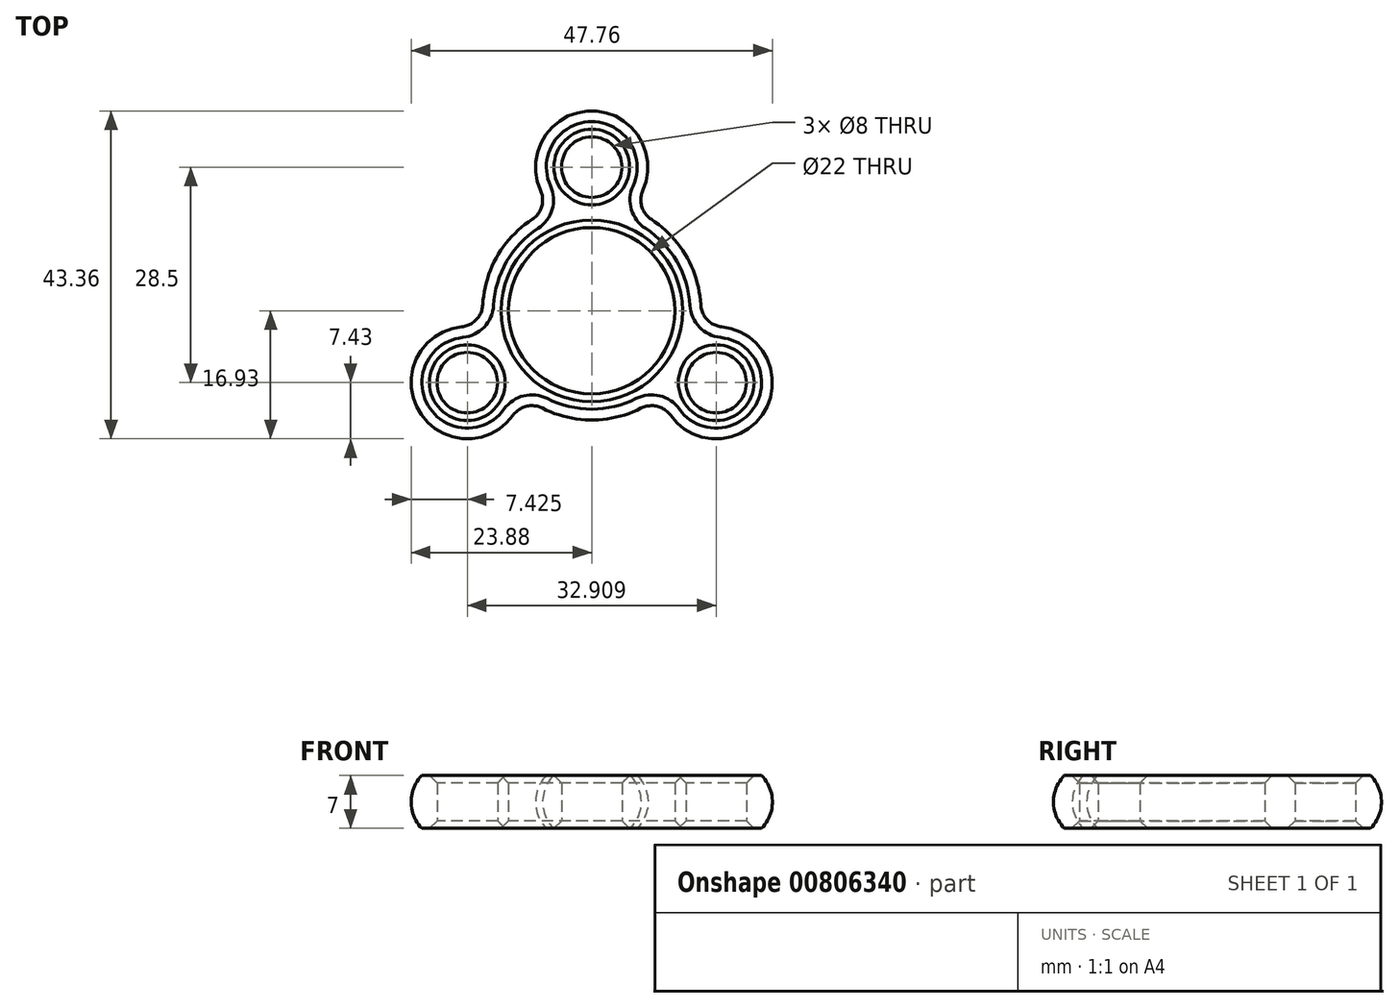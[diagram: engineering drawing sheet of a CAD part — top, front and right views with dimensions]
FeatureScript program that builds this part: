
annotation { "Feature Type Name" : "Feature", "Feature Type Description" : "" }
export const myFeature = defineFeature(function(context is Context, id is Id, definition is map)
    precondition{}
    {
        {
            var Q0;
            Q0=qCreatedBy(makeId("Top.planeOp"),FACE);
            var sketch = newSketch(context, id + "F0", { "sketchPlane" : qUnion([Q0])});
            skCircle(sketch, "E0", {"center": v(0, 0) * mm, "radius": 11 * mm});
            skCircle(sketch, "E1", {"center": v(0, 0) * mm, "radius": 13 * mm});
            skCircle(sketch, "E2", {"center": v(0, 19) * mm, "radius": 4 * mm});
            skCircle(sketch, "E3", {"center": v(0, 19) * mm, "radius": 6 * mm});
            skCircle(sketch, "E4.1.0", {"center": v(-16.45, -9.5) * mm, "radius": 6 * mm});
            skCircle(sketch, "E4.1.1", {"center": v(-16.45, -9.5) * mm, "radius": 4 * mm});
            skCircle(sketch, "E4.2.0", {"center": v(16.45, -9.5) * mm, "radius": 6 * mm});
            skCircle(sketch, "E4.2.1", {"center": v(16.45, -9.5) * mm, "radius": 4 * mm});
            skCircle(sketch, "E5", {"center": v(-9.56, 14.66) * mm, "radius": 4.5 * mm});
            skCircle(sketch, "E6", {"center": v(9.56, 14.66) * mm, "radius": 4.5 * mm});
            skCircle(sketch, "E7.1.0", {"center": v(-7.91, -15.6) * mm, "radius": 4.5 * mm});
            skCircle(sketch, "E7.1.1", {"center": v(-17.47, 0.95) * mm, "radius": 4.5 * mm});
            skCircle(sketch, "E7.2.0", {"center": v(17.47, 0.95) * mm, "radius": 4.5 * mm});
            skCircle(sketch, "E7.2.1", {"center": v(7.91, -15.6) * mm, "radius": 4.5 * mm});
            skSolve(sketch);
        }
        {
            var Q0;
            {var subQ0=sQuery(id+"F0.wireOp",EDGE,"E6");var subQ1=sQuery(id+"F0.wireOp",EDGE,"E1");var subQ2=makeQuery(id+"F0.imprint","INTERSECT",VERTEX,{"derivedFrom":[subQ1,subQ0]});Q0=makeQuery(id+"F0.imprint","IMPRINT",FACE,{"disambiguationData":[TD([[makeQuery(id+"F0.imprint","IMPRINT",EDGE,{"disambiguationData":[TD([[subQ2,-1.0]])],"derivedFrom":subQ1}),-1.0]])]});}
            var Q1;
            {var subQ0=sQuery(id+"F0.wireOp",EDGE,"E3");var subQ1=sQuery(id+"F0.wireOp",EDGE,"E1");var subQ2=makeQuery(id+"F0.imprint","INTERSECT",VERTEX,{"derivedFrom":[subQ1,subQ0]});Q1=makeQuery(id+"F0.imprint","IMPRINT",FACE,{"disambiguationData":[TD([[makeQuery(id+"F0.imprint","IMPRINT",EDGE,{"disambiguationData":[TD([[subQ2,-1.0]])],"derivedFrom":subQ1}),-1.0]])]});}
            var Q2;
            {var subQ0=sQuery(id+"F0.wireOp",EDGE,"E7.1.1");var subQ1=sQuery(id+"F0.wireOp",EDGE,"E1");var subQ2=makeQuery(id+"F0.imprint","INTERSECT",VERTEX,{"derivedFrom":[subQ1,subQ0]});Q2=makeQuery(id+"F0.imprint","IMPRINT",FACE,{"disambiguationData":[TD([[makeQuery(id+"F0.imprint","IMPRINT",EDGE,{"disambiguationData":[TD([[subQ2,-1.0]])],"derivedFrom":subQ1}),-1.0]])]});}
            var Q3;
            {var subQ0=sQuery(id+"F0.wireOp",EDGE,"E4.1.0");var subQ1=sQuery(id+"F0.wireOp",EDGE,"E1");var subQ2=makeQuery(id+"F0.imprint","INTERSECT",VERTEX,{"derivedFrom":[subQ1,subQ0]});Q3=makeQuery(id+"F0.imprint","IMPRINT",FACE,{"disambiguationData":[TD([[makeQuery(id+"F0.imprint","IMPRINT",EDGE,{"disambiguationData":[TD([[subQ2,-1.0]])],"derivedFrom":subQ1}),-1.0]])]});}
            var Q4;
            {var subQ0=sQuery(id+"F0.wireOp",EDGE,"E7.2.1");var subQ1=sQuery(id+"F0.wireOp",EDGE,"E1");var subQ2=makeQuery(id+"F0.imprint","INTERSECT",VERTEX,{"derivedFrom":[subQ1,subQ0]});Q4=makeQuery(id+"F0.imprint","IMPRINT",FACE,{"disambiguationData":[TD([[makeQuery(id+"F0.imprint","IMPRINT",EDGE,{"disambiguationData":[TD([[subQ2,-1.0]])],"derivedFrom":subQ1}),-1.0]])]});}
            var Q5;
            {var subQ0=sQuery(id+"F0.wireOp",EDGE,"E7.2.0");var subQ1=sQuery(id+"F0.wireOp",EDGE,"E1");var subQ2=makeQuery(id+"F0.imprint","INTERSECT",VERTEX,{"derivedFrom":[subQ1,subQ0]});Q5=makeQuery(id+"F0.imprint","IMPRINT",FACE,{"disambiguationData":[TD([[makeQuery(id+"F0.imprint","IMPRINT",EDGE,{"disambiguationData":[TD([[subQ2,1.0]])],"derivedFrom":subQ1}),-1.0]])]});}
            var Q6;
            Q6=makeQuery(id+"F0.imprint","IMPRINT",FACE,{"disambiguationData":[TD([[makeQuery(id+"F0.imprint","IMPRINT",EDGE,{"derivedFrom":sQuery(id+"F0.wireOp",EDGE,"E0")}),-1.0]])]});
            var Q7;
            Q7=makeQuery(id+"F0.imprint","IMPRINT",FACE,{"disambiguationData":[TD([[makeQuery(id+"F0.imprint","IMPRINT",EDGE,{"derivedFrom":sQuery(id+"F0.wireOp",EDGE,"E2")}),-1.0]])]});
            var Q8;
            Q8=makeQuery(id+"F0.imprint","IMPRINT",FACE,{"disambiguationData":[TD([[makeQuery(id+"F0.imprint","IMPRINT",EDGE,{"derivedFrom":sQuery(id+"F0.wireOp",EDGE,"E4.1.1")}),-1.0]])]});
            var Q9;
            Q9=makeQuery(id+"F0.imprint","IMPRINT",FACE,{"disambiguationData":[TD([[makeQuery(id+"F0.imprint","IMPRINT",EDGE,{"derivedFrom":sQuery(id+"F0.wireOp",EDGE,"E4.2.1")}),-1.0]])]});
            extrude(context, id + "F1", {"entities" : qUnion([Q0, Q1, Q2, Q3, Q4, Q5, Q6, Q7, Q8, Q9]), "endBound" : BoundingType.SYMMETRIC, "depth" : 7 * mm, "offsetDistance" : 25.4 * mm});
        }
        {
            var Q0;
            Q0=qCreatedBy(makeId("Right.planeOp"),FACE);
            var sketch = newSketch(context, id + "F2", { "sketchPlane" : qUnion([Q0])});
            skLineSegment(sketch, "E8", {"start": v(25, 3.5) * mm, "end": v(25, -3.5) * mm});
            skArc(sketch, "E9", {"start": v(25, -3.5) * mm, "mid": v(26.43, 0) * mm, "end": v(25, 3.5) * mm});
            skSolve(sketch);
        }
        {
            var Q0;
            Q0=makeQuery(id+"F2.imprint","IMPRINT",FACE,{"disambiguationData":[TD([[makeQuery(id+"F2.imprint","IMPRINT",EDGE,{"derivedFrom":sQuery(id+"F2.wireOp",EDGE,"E8")}),1.0]])]});
            var Q1;
            Q1=makeQuery(id+"F1.opExtrude","CAP_EDGE",EDGE,{"disambiguationData":[OSD([sQuery(id+"F0.wireOp",EDGE,"E3")])],"isStart":false});
            var Q2;
            Q2=makeQuery(id+"F1.opExtrude","CAP_EDGE",EDGE,{"disambiguationData":[OSD([sQuery(id+"F0.wireOp",EDGE,"E5")])],"isStart":false});
            var Q3;
            {var subQ0=sQuery(id+"F0.wireOp",EDGE,"E1");Q3=makeQuery(id+"F1.opExtrude","CAP_EDGE",EDGE,{"disambiguationData":[OSD([subQ0]),TDD([makeQuery(id+"F0.imprint","IMPRINT",EDGE,{"disambiguationData":[TD([[makeQuery(id+"F0.imprint","INTERSECT",VERTEX,{"derivedFrom":[subQ0,sQuery(id+"F0.wireOp",EDGE,"E5")]}),-1.0]])],"derivedFrom":subQ0})])],"isStart":false});}
            var Q4;
            Q4=makeQuery(id+"F1.opExtrude","CAP_EDGE",EDGE,{"disambiguationData":[OSD([sQuery(id+"F0.wireOp",EDGE,"E7.1.1")])],"isStart":false});
            var Q5;
            Q5=makeQuery(id+"F1.opExtrude","CAP_EDGE",EDGE,{"disambiguationData":[OSD([sQuery(id+"F0.wireOp",EDGE,"E4.1.0")])],"isStart":false});
            var Q6;
            Q6=makeQuery(id+"F1.opExtrude","CAP_EDGE",EDGE,{"disambiguationData":[OSD([sQuery(id+"F0.wireOp",EDGE,"E7.1.0")])],"isStart":false});
            var Q7;
            {var subQ0=sQuery(id+"F0.wireOp",EDGE,"E1");Q7=makeQuery(id+"F1.opExtrude","CAP_EDGE",EDGE,{"disambiguationData":[OSD([subQ0]),TDD([makeQuery(id+"F0.imprint","IMPRINT",EDGE,{"disambiguationData":[TD([[makeQuery(id+"F0.imprint","INTERSECT",VERTEX,{"derivedFrom":[subQ0,sQuery(id+"F0.wireOp",EDGE,"E7.1.0")]}),-1.0]])],"derivedFrom":subQ0})])],"isStart":false});}
            var Q8;
            Q8=makeQuery(id+"F1.opExtrude","CAP_EDGE",EDGE,{"disambiguationData":[OSD([sQuery(id+"F0.wireOp",EDGE,"E7.2.1")])],"isStart":false});
            var Q9;
            Q9=makeQuery(id+"F1.opExtrude","CAP_EDGE",EDGE,{"disambiguationData":[OSD([sQuery(id+"F0.wireOp",EDGE,"E4.2.0")])],"isStart":false});
            var Q10;
            Q10=makeQuery(id+"F1.opExtrude","CAP_EDGE",EDGE,{"disambiguationData":[OSD([sQuery(id+"F0.wireOp",EDGE,"E7.2.0")])],"isStart":false});
            var Q11;
            {var subQ0=sQuery(id+"F0.wireOp",EDGE,"E1");Q11=makeQuery(id+"F1.opExtrude","CAP_EDGE",EDGE,{"disambiguationData":[OSD([subQ0]),TDD([makeQuery(id+"F0.imprint","IMPRINT",EDGE,{"disambiguationData":[TD([[makeQuery(id+"F0.imprint","INTERSECT",VERTEX,{"derivedFrom":[subQ0,sQuery(id+"F0.wireOp",EDGE,"E6")]}),1.0]])],"derivedFrom":subQ0})])],"isStart":false});}
            var Q12;
            Q12=makeQuery(id+"F1.opExtrude","CAP_EDGE",EDGE,{"disambiguationData":[OSD([sQuery(id+"F0.wireOp",EDGE,"E6")])],"isStart":false});
            sweep(context, id + "F3", {"operationType" : NewBodyOperationType.ADD, "profiles" : qUnion([Q0]), "path" : qUnion([Q1, Q2, Q3, Q4, Q5, Q6, Q7, Q8, Q9, Q10, Q11, Q12])});
        }
        {
            var Q0;
            Q0=makeQuery(id+"F1.opExtrude","CAP_EDGE",EDGE,{"disambiguationData":[OSD([sQuery(id+"F0.wireOp",EDGE,"E2")])],"isStart":false});
            var Q1;
            Q1=makeQuery(id+"F1.opExtrude","CAP_EDGE",EDGE,{"disambiguationData":[OSD([sQuery(id+"F0.wireOp",EDGE,"E0")])],"isStart":false});
            var Q2;
            Q2=makeQuery(id+"F1.opExtrude","CAP_EDGE",EDGE,{"disambiguationData":[OSD([sQuery(id+"F0.wireOp",EDGE,"E4.1.1")])],"isStart":false});
            var Q3;
            Q3=makeQuery(id+"F1.opExtrude","CAP_EDGE",EDGE,{"disambiguationData":[OSD([sQuery(id+"F0.wireOp",EDGE,"E4.2.1")])],"isStart":false});
            var Q4;
            Q4=makeQuery(id+"F1.opExtrude","CAP_EDGE",EDGE,{"disambiguationData":[OSD([sQuery(id+"F0.wireOp",EDGE,"E4.1.1")])],"isStart":true});
            var Q5;
            Q5=makeQuery(id+"F1.opExtrude","CAP_EDGE",EDGE,{"disambiguationData":[OSD([sQuery(id+"F0.wireOp",EDGE,"E0")])],"isStart":true});
            var Q6;
            Q6=makeQuery(id+"F1.opExtrude","CAP_EDGE",EDGE,{"disambiguationData":[OSD([sQuery(id+"F0.wireOp",EDGE,"E4.2.1")])],"isStart":true});
            var Q7;
            Q7=makeQuery(id+"F1.opExtrude","CAP_EDGE",EDGE,{"disambiguationData":[OSD([sQuery(id+"F0.wireOp",EDGE,"E2")])],"isStart":true});
            chamfer(context, id + "F4", {"entities" : qUnion([Q0, Q1, Q2, Q3, Q4, Q5, Q6, Q7]), "width" : 1 * mm, "tangentPropagation" : true});
        }
    });
